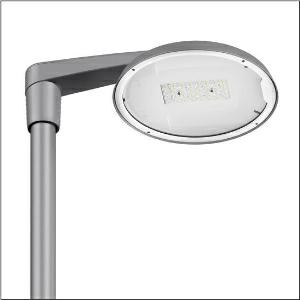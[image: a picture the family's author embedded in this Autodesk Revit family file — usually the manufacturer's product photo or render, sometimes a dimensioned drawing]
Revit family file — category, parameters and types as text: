
# Revit family: dl_r__50_iq_mini___st0_5a_5xa248b31f08fe_5b8c
name_source: partatom
category: Lighting Fixtures
units: mm (PartAtom-declared; Revit-internal decimal feet)

## family parameters
Cut with Voids When Loaded = No
Host = Face
Light Source = No
Part Type = Normal
Room Calculation Point = No
Round Connector Dimension = Use Diameter
Shared = No

## types (1)
- --- (1 x LED, 2700 lm, 16.3 W, 3000K)
    Apparent Load = 16 VA
    CIE Flux Codes = 41 75 97 100 100
    Color Rendering = 70
    Color Temperature = 3000K
    Default Elevation = 1800 mm
    Description = DL® 50 iQ mini, mast luminaire, primary light control with lens, of PMMA, primary optical cover: cover, of toughened safety glass, transparent, light distribution: ST0.5a, light emission: direct distribution, primary light characteristic: asymmetric, installation type: side-entry, post-top, LED, High Power LED, rated luminous flux: 2.700lm, luminous efficacy: 166lm/W, light colour: 730, colour temperature: 3000K, control: optimised constant luminous flux control (CLO 2.0), Desk-Remote (wireless, voltage-free reading and setting of iQ features in the workshop via application-optimized NFC function/RFID function), Light-Fading, Smart-Wire, Night-Set, Lumen-Switch, Temp-Guard, Auto-Match, Street-Remote, mains connection: 230..240V, AC, 50/60Hz, connection cable pre-assembled, cable length: 6,5m, start of lifetime: 16W, end of service life: 17W, reduction: 8W, luminaire housing, of diecast aluminium, powder-coated, Siteco® metallic grey (DB 702S), inclination adjustable: 0°, 5°, 10° (post-top) | 0°, -5°, -10°, -15° (side-entry), please order mast post-top element or mast side-entry element separately, diameter: 500mm, height: 115mm, post-top: for spigot size d x l = 76 x 100mm; with reducer (optional accessory) 60 x 100mm | side-entry: for spigot size d x l = 60 x 100mm; with reducer (optional accessory) 42 x 100mm, protection rating (complete): IP66, insulation class (complete): insulation class II (safety insulation), certification: CE, ENEC, ENEC+, VDE, impact resistance: IK08, permissible operating ambient temperature for outdoor applications: -25..+40°C, standard-compliant lighting for roads and squares, packaging unit: 1 piece

Light Distribution: ST0.5a
    Height = 115 mm
    Lamp = 1 x LED
    Lamp Light Flux = 2700 lm
    Lamp Power = 16.3 W
    Lamp count = 1
    Length = 500 mm
    Luminous efficacy = 166 lm/W
    Manufacturer = Siteco
    ModVariant = No
    Model = 5XA248B31F08FE
    Number of Poles = 1
    OnlyDefault = Yes
    Power Factor = 1
    Product Name = DL® 50 iQ mini | ST0.5a
    Product group = mast luminaire | pylon top
    ProductGroupID = 6100
    Protection Class = Protection class II
    Protection Degree = IP 66
    RLX_Detail_Level = 1
    RLX_Emergency_Light_Flux = 0 lm
    RLX_Emergency_Type = 0
    RLX_Emergency_Type_DB = No
    RlxData = <blob elided: 126581 chars, md5=28842240>
    Socket = socket
    Standby Power = 0 W
    System Light Flux = 2700 lm
    System Power = 16 W
    Type Comments = factory setting: luminous flux: 100 % | dim-lin: 254 | 333 mA
    Type Image = l_1251794.jpg
    URL = http://relux.com
    VarID = @adj_109233
    Voltage = 0 V
    Weight = 0.00 kg
    Width = 0 mm  [stored 0 ft]

note: [stored X ft] marks values corroborated as IEEE doubles in the binary element streams (Revit-internal decimal feet)

## geometry (parser evidence)
native form markers: Blend x4, Sweep x8
no freeform markers — native parametric forms only
